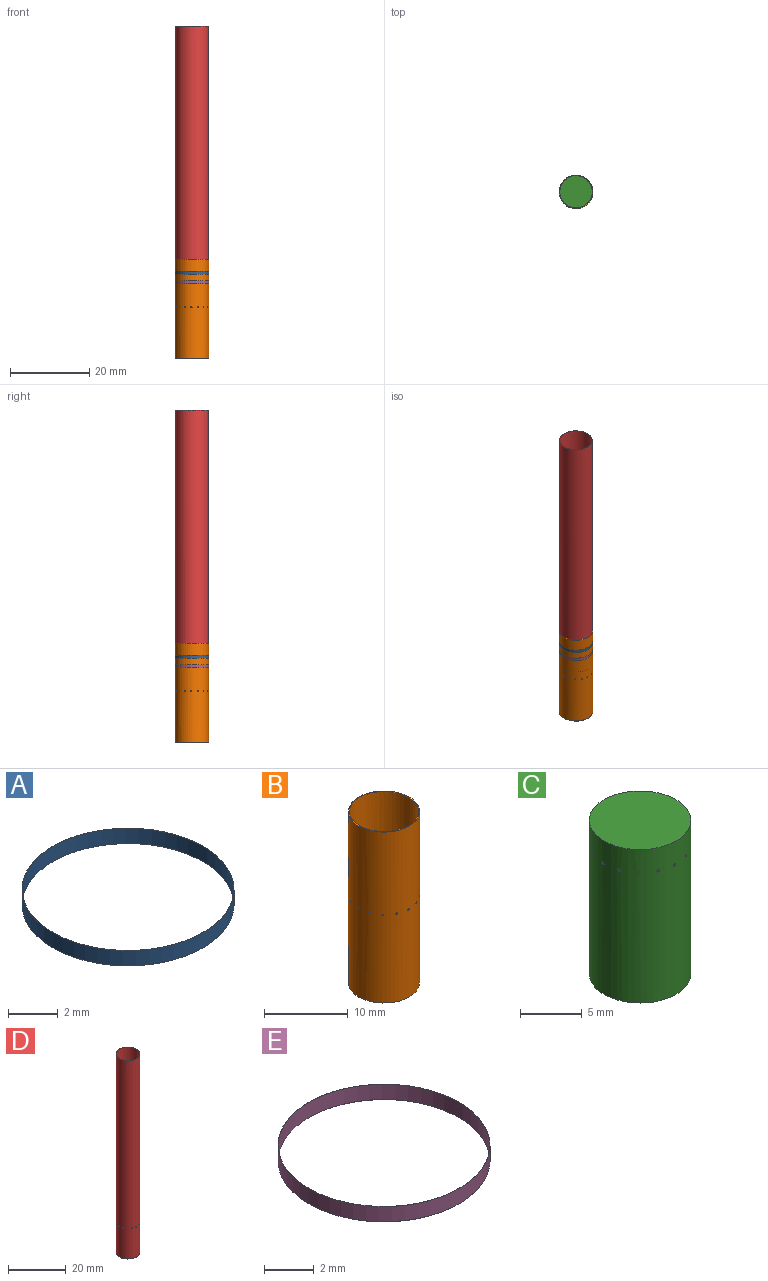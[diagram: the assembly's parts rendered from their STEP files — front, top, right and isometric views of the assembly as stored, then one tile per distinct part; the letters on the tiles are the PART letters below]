
ASSEMBLY  parts=5 mates=4
PART A: 4 faces, bbox 8.5x8.5x0.8 mm
  f0: cylinder r=4.25mm len=8.5mm, axis (0,0,-1), area 20mm2, adj f2,f3
  f1: cylinder r=4.26mm len=8.52mm, axis (0,0,-1), area 20.1mm2, adj f2,f3
  f2: plane 8.52x8.52mm, normal (0,0,1), area 0.3mm2, adj f0,f1
  f3: plane 8.52x8.52mm, normal (0,0,-1), area 0.3mm2, adj f0,f1
PART B: 68 faces, bbox 8.5x8.5x25 mm
  f0: cylinder r=4.14mm len=25mm, axis (0,0,-1), area 649.5mm2, adj f2,f3,f4,f5,f6,f7,f8,f9
  f1: cylinder r=4.25mm len=25mm, axis (0,0,-1), area 666.8mm2, adj f2,f3,f4,f5,f6,f7,f8,f9
  f2: plane 8.5x8.5mm, normal (0,0,1), area 2.9mm2, adj f0,f1
  f3: plane 8.5x8.5mm, normal (0,0,-1), area 2.9mm2, adj f0,f1
  f4: cylinder r=0.16mm len=0.15mm, axis (-0.07,-1,0), area 0mm2, adj f0,f1,f5,f6
  f5: cylinder r=0.16mm len=0.15mm, axis (0.07,1,0), area 0mm2, adj f0,f1,f4,f7
  f6: cylinder r=0.16mm len=0.14mm, axis (0,1,0), area 0mm2, adj f0,f1,f4,f7
  f7: cylinder r=0.16mm len=0.14mm, axis (0,-1,0), area 0mm2, adj f0,f1,f5,f6
  f8: cylinder r=0.16mm len=0.18mm, axis (-0.45,-0.89,0), area 0mm2, adj f0,f1,f9,f10
  f9: cylinder r=0.16mm len=0.18mm, axis (0.45,0.89,0), area 0mm2, adj f0,f1,f8,f11
  f10: cylinder r=0.16mm len=0.18mm, axis (0.38,0.92,0), area 0mm2, adj f0,f1,f8,f11
  f11: cylinder r=0.16mm len=0.18mm, axis (-0.38,-0.92,0), area 0mm2, adj f0,f1,f9,f10
  f12: cylinder r=0.16mm len=0.18mm, axis (-0.75,-0.66,0), area 0mm2, adj f0,f1,f13,f14
  f13: cylinder r=0.16mm len=0.18mm, axis (0.75,0.66,0), area 0mm2, adj f0,f1,f12,f15
  f14: cylinder r=0.16mm len=0.18mm, axis (0.71,0.71,0), area 0mm2, adj f0,f1,f12,f15
  f15: cylinder r=0.16mm len=0.18mm, axis (-0.71,-0.71,0), area 0mm2, adj f0,f1,f13,f14
  f16: cylinder r=0.16mm len=0.17mm, axis (-0.95,-0.32,0), area 0mm2, adj f0,f1,f17,f18
  f17: cylinder r=0.16mm len=0.17mm, axis (0.95,0.32,0), area 0mm2, adj f0,f1,f16,f19
  f18: cylinder r=0.16mm len=0.18mm, axis (0.92,0.38,0), area 0mm2, adj f0,f1,f16,f19
  f19: cylinder r=0.16mm len=0.18mm, axis (-0.92,-0.38,0), area 0mm2, adj f0,f1,f17,f18
  f20: cylinder r=0.16mm len=0.15mm, axis (-1,0.07,0), area 0mm2, adj f0,f1,f21,f22
  f21: cylinder r=0.16mm len=0.15mm, axis (1,-0.07,0), area 0mm2, adj f0,f1,f20,f23
  f22: cylinder r=0.16mm len=0.14mm, axis (1,0,0), area 0mm2, adj f0,f1,f20,f23
  f23: cylinder r=0.16mm len=0.14mm, axis (-1,0,0), area 0mm2, adj f0,f1,f21,f22
  f24: cylinder r=0.16mm len=0.18mm, axis (-0.89,0.45,0), area 0mm2, adj f0,f1,f25,f26
  f25: cylinder r=0.16mm len=0.18mm, axis (0.89,-0.45,0), area 0mm2, adj f0,f1,f24,f27
  f26: cylinder r=0.16mm len=0.18mm, axis (0.92,-0.38,0), area 0mm2, adj f0,f1,f24,f27
  f27: cylinder r=0.16mm len=0.18mm, axis (-0.92,0.38,0), area 0mm2, adj f0,f1,f25,f26
  f28: cylinder r=0.16mm len=0.18mm, axis (-0.66,0.75,0), area 0mm2, adj f0,f1,f29,f30
  f29: cylinder r=0.16mm len=0.18mm, axis (0.66,-0.75,0), area 0mm2, adj f0,f1,f28,f31
  f30: cylinder r=0.16mm len=0.18mm, axis (0.71,-0.71,0), area 0mm2, adj f0,f1,f28,f31
  f31: cylinder r=0.16mm len=0.18mm, axis (-0.71,0.71,0), area 0mm2, adj f0,f1,f29,f30
  f32: cylinder r=0.16mm len=0.17mm, axis (-0.32,0.95,0), area 0mm2, adj f0,f1,f33,f34
  f33: cylinder r=0.16mm len=0.17mm, axis (0.32,-0.95,0), area 0mm2, adj f0,f1,f32,f35
  f34: cylinder r=0.16mm len=0.18mm, axis (0.38,-0.92,0), area 0mm2, adj f0,f1,f32,f35
  f35: cylinder r=0.16mm len=0.18mm, axis (-0.38,0.92,0), area 0mm2, adj f0,f1,f33,f34
  f36: cylinder r=0.16mm len=0.15mm, axis (0.07,1,0), area 0mm2, adj f0,f1,f37,f38
  f37: cylinder r=0.16mm len=0.15mm, axis (-0.07,-1,0), area 0mm2, adj f0,f1,f36,f39
  f38: cylinder r=0.16mm len=0.14mm, axis (0,-1,0), area 0mm2, adj f0,f1,f36,f39
  f39: cylinder r=0.16mm len=0.14mm, axis (0,1,0), area 0mm2, adj f0,f1,f37,f38
  f40: cylinder r=0.16mm len=0.18mm, axis (0.45,0.89,0), area 0mm2, adj f0,f1,f41,f42
  f41: cylinder r=0.16mm len=0.18mm, axis (-0.45,-0.89,0), area 0mm2, adj f0,f1,f40,f43
  f42: cylinder r=0.16mm len=0.18mm, axis (-0.38,-0.92,0), area 0mm2, adj f0,f1,f40,f43
  f43: cylinder r=0.16mm len=0.18mm, axis (0.38,0.92,0), area 0mm2, adj f0,f1,f41,f42
  f44: cylinder r=0.16mm len=0.18mm, axis (0.75,0.66,0), area 0mm2, adj f0,f1,f45,f46
  f45: cylinder r=0.16mm len=0.18mm, axis (-0.75,-0.66,0), area 0mm2, adj f0,f1,f44,f47
  f46: cylinder r=0.16mm len=0.18mm, axis (-0.71,-0.71,0), area 0mm2, adj f0,f1,f44,f47
  f47: cylinder r=0.16mm len=0.18mm, axis (0.71,0.71,0), area 0mm2, adj f0,f1,f45,f46
  f48: cylinder r=0.16mm len=0.17mm, axis (0.95,0.32,0), area 0mm2, adj f0,f1,f49,f50
  f49: cylinder r=0.16mm len=0.17mm, axis (-0.95,-0.32,0), area 0mm2, adj f0,f1,f48,f51
  f50: cylinder r=0.16mm len=0.18mm, axis (-0.92,-0.38,0), area 0mm2, adj f0,f1,f48,f51
  f51: cylinder r=0.16mm len=0.18mm, axis (0.92,0.38,0), area 0mm2, adj f0,f1,f49,f50
  f52: cylinder r=0.16mm len=0.15mm, axis (1,-0.07,0), area 0mm2, adj f0,f1,f53,f54
  f53: cylinder r=0.16mm len=0.15mm, axis (-1,0.07,0), area 0mm2, adj f0,f1,f52,f55
  f54: cylinder r=0.16mm len=0.14mm, axis (-1,0,0), area 0mm2, adj f0,f1,f52,f55
  f55: cylinder r=0.16mm len=0.14mm, axis (1,0,0), area 0mm2, adj f0,f1,f53,f54
  f56: cylinder r=0.16mm len=0.18mm, axis (0.89,-0.45,0), area 0mm2, adj f0,f1,f57,f58
  f57: cylinder r=0.16mm len=0.18mm, axis (-0.89,0.45,0), area 0mm2, adj f0,f1,f56,f59
  f58: cylinder r=0.16mm len=0.18mm, axis (-0.92,0.38,0), area 0mm2, adj f0,f1,f56,f59
  f59: cylinder r=0.16mm len=0.18mm, axis (0.92,-0.38,0), area 0mm2, adj f0,f1,f57,f58
  f60: cylinder r=0.16mm len=0.18mm, axis (0.66,-0.75,0), area 0mm2, adj f0,f1,f61,f62
  f61: cylinder r=0.16mm len=0.18mm, axis (-0.66,0.75,0), area 0mm2, adj f0,f1,f60,f63
  f62: cylinder r=0.16mm len=0.18mm, axis (-0.71,0.71,0), area 0mm2, adj f0,f1,f60,f63
  f63: cylinder r=0.16mm len=0.18mm, axis (0.71,-0.71,0), area 0mm2, adj f0,f1,f61,f62
  f64: cylinder r=0.16mm len=0.17mm, axis (0.32,-0.95,0), area 0mm2, adj f0,f1,f65,f66
  f65: cylinder r=0.16mm len=0.17mm, axis (-0.32,0.95,0), area 0mm2, adj f0,f1,f64,f67
  f66: cylinder r=0.16mm len=0.18mm, axis (-0.38,0.92,0), area 0mm2, adj f0,f1,f64,f67
  f67: cylinder r=0.16mm len=0.18mm, axis (0.38,-0.92,0), area 0mm2, adj f0,f1,f65,f66
PART C: 83 faces, bbox 8.2x8.2x15.2 mm
  f0: cylinder r=4.1mm len=15.15mm, axis (0,0,1), area 389.5mm2, adj f1,f2,f4,f5,f6,f7,f9,f10
  f1: plane 8.2x8.2mm, normal (0,0,-1), area 52.8mm2, adj f0
  f2: plane 8.2x8.2mm, normal (0,0,1), area 52.8mm2, adj f0
  f3: cylinder r=4.05mm len=0.27mm, axis (0,0,1), area 0mm2, adj f4,f5,f6,f7
  f4: cylinder r=0.16mm len=0.14mm, axis (-0.07,-1,0), area 0mm2, adj f0,f3,f5,f6
  f5: cylinder r=0.16mm len=0.14mm, axis (0.07,1,0), area 0mm2, adj f0,f3,f4,f7
  f6: cylinder r=0.16mm len=0.14mm, axis (0,1,0), area 0mm2, adj f0,f3,f4,f7
  f7: cylinder r=0.16mm len=0.14mm, axis (0,-1,0), area 0mm2, adj f0,f3,f5,f6
  f8: cylinder r=4.05mm len=0.25mm, axis (0,0,1), area 0mm2, adj f9,f10,f11,f12
  f9: cylinder r=0.16mm len=0.15mm, axis (-0.45,-0.89,0), area 0mm2, adj f0,f8,f10,f11
  f10: cylinder r=0.16mm len=0.15mm, axis (0.45,0.89,0), area 0mm2, adj f0,f8,f9,f12
  f11: cylinder r=0.16mm len=0.15mm, axis (0.38,0.92,0), area 0mm2, adj f0,f8,f9,f12
  f12: cylinder r=0.16mm len=0.15mm, axis (-0.38,-0.92,0), area 0mm2, adj f0,f8,f10,f11
  f13: cylinder r=4.05mm len=0.25mm, axis (0,0,1), area 0mm2, adj f14,f15,f16,f17
  f14: cylinder r=0.16mm len=0.14mm, axis (-0.75,-0.66,0), area 0mm2, adj f0,f13,f15,f16
  f15: cylinder r=0.16mm len=0.14mm, axis (0.75,0.66,0), area 0mm2, adj f0,f13,f14,f17
  f16: cylinder r=0.16mm len=0.14mm, axis (0.71,0.71,0), area 0mm2, adj f0,f13,f14,f17
  f17: cylinder r=0.16mm len=0.14mm, axis (-0.71,-0.71,0), area 0mm2, adj f0,f13,f15,f16
  f18: cylinder r=4.05mm len=0.26mm, axis (0,0,1), area 0mm2, adj f19,f20,f21,f22
  f19: cylinder r=0.16mm len=0.15mm, axis (-0.95,-0.32,0), area 0mm2, adj f0,f18,f20,f21
  f20: cylinder r=0.16mm len=0.15mm, axis (0.95,0.32,0), area 0mm2, adj f0,f18,f19,f22
  f21: cylinder r=0.16mm len=0.15mm, axis (0.92,0.38,0), area 0mm2, adj f0,f18,f19,f22
  f22: cylinder r=0.16mm len=0.15mm, axis (-0.92,-0.38,0), area 0mm2, adj f0,f18,f20,f21
  f23: cylinder r=4.05mm len=0.27mm, axis (0,0,1), area 0mm2, adj f24,f25,f26,f27
  f24: cylinder r=0.16mm len=0.14mm, axis (-1,0.07,0), area 0mm2, adj f0,f23,f25,f26
  f25: cylinder r=0.16mm len=0.14mm, axis (1,-0.07,0), area 0mm2, adj f0,f23,f24,f27
  f26: cylinder r=0.16mm len=0.14mm, axis (1,0,0), area 0mm2, adj f0,f23,f24,f27
  f27: cylinder r=0.16mm len=0.14mm, axis (-1,0,0), area 0mm2, adj f0,f23,f25,f26
  f28: cylinder r=4.05mm len=0.25mm, axis (0,0,1), area 0mm2, adj f29,f30,f31,f32
  f29: cylinder r=0.16mm len=0.15mm, axis (-0.89,0.45,0), area 0mm2, adj f0,f28,f30,f31
  f30: cylinder r=0.16mm len=0.15mm, axis (0.89,-0.45,0), area 0mm2, adj f0,f28,f29,f32
  f31: cylinder r=0.16mm len=0.15mm, axis (0.92,-0.38,0), area 0mm2, adj f0,f28,f29,f32
  f32: cylinder r=0.16mm len=0.15mm, axis (-0.92,0.38,0), area 0mm2, adj f0,f28,f30,f31
  f33: cylinder r=4.05mm len=0.25mm, axis (0,0,1), area 0mm2, adj f34,f35,f36,f37
  f34: cylinder r=0.16mm len=0.14mm, axis (-0.66,0.75,0), area 0mm2, adj f0,f33,f35,f36
  f35: cylinder r=0.16mm len=0.14mm, axis (0.66,-0.75,0), area 0mm2, adj f0,f33,f34,f37
  f36: cylinder r=0.16mm len=0.14mm, axis (0.71,-0.71,0), area 0mm2, adj f0,f33,f34,f37
  f37: cylinder r=0.16mm len=0.14mm, axis (-0.71,0.71,0), area 0mm2, adj f0,f33,f35,f36
  f38: cylinder r=4.05mm len=0.26mm, axis (0,0,1), area 0mm2, adj f39,f40,f41,f42
  f39: cylinder r=0.16mm len=0.15mm, axis (-0.32,0.95,0), area 0mm2, adj f0,f38,f40,f41
  f40: cylinder r=0.16mm len=0.15mm, axis (0.32,-0.95,0), area 0mm2, adj f0,f38,f39,f42
  f41: cylinder r=0.16mm len=0.15mm, axis (0.38,-0.92,0), area 0mm2, adj f0,f38,f39,f42
  f42: cylinder r=0.16mm len=0.15mm, axis (-0.38,0.92,0), area 0mm2, adj f0,f38,f40,f41
  f43: cylinder r=4.05mm len=0.27mm, axis (0,0,1), area 0mm2, adj f44,f45,f46,f47
  f44: cylinder r=0.16mm len=0.14mm, axis (0.07,1,0), area 0mm2, adj f0,f43,f45,f46
  f45: cylinder r=0.16mm len=0.14mm, axis (-0.07,-1,0), area 0mm2, adj f0,f43,f44,f47
  f46: cylinder r=0.16mm len=0.14mm, axis (0,-1,0), area 0mm2, adj f0,f43,f44,f47
  f47: cylinder r=0.16mm len=0.14mm, axis (0,1,0), area 0mm2, adj f0,f43,f45,f46
  f48: cylinder r=4.05mm len=0.25mm, axis (0,0,1), area 0mm2, adj f49,f50,f51,f52
  f49: cylinder r=0.16mm len=0.15mm, axis (0.45,0.89,0), area 0mm2, adj f0,f48,f50,f51
  f50: cylinder r=0.16mm len=0.15mm, axis (-0.45,-0.89,0), area 0mm2, adj f0,f48,f49,f52
  f51: cylinder r=0.16mm len=0.15mm, axis (-0.38,-0.92,0), area 0mm2, adj f0,f48,f49,f52
  f52: cylinder r=0.16mm len=0.15mm, axis (0.38,0.92,0), area 0mm2, adj f0,f48,f50,f51
  f53: cylinder r=4.05mm len=0.25mm, axis (0,0,1), area 0mm2, adj f54,f55,f56,f57
  f54: cylinder r=0.16mm len=0.14mm, axis (0.75,0.66,0), area 0mm2, adj f0,f53,f55,f56
  f55: cylinder r=0.16mm len=0.14mm, axis (-0.75,-0.66,0), area 0mm2, adj f0,f53,f54,f57
  f56: cylinder r=0.16mm len=0.14mm, axis (-0.71,-0.71,0), area 0mm2, adj f0,f53,f54,f57
  f57: cylinder r=0.16mm len=0.14mm, axis (0.71,0.71,0), area 0mm2, adj f0,f53,f55,f56
  f58: cylinder r=4.05mm len=0.26mm, axis (0,0,1), area 0mm2, adj f59,f60,f61,f62
  f59: cylinder r=0.16mm len=0.15mm, axis (0.95,0.32,0), area 0mm2, adj f0,f58,f60,f61
  f60: cylinder r=0.16mm len=0.15mm, axis (-0.95,-0.32,0), area 0mm2, adj f0,f58,f59,f62
  f61: cylinder r=0.16mm len=0.15mm, axis (-0.92,-0.38,0), area 0mm2, adj f0,f58,f59,f62
  f62: cylinder r=0.16mm len=0.15mm, axis (0.92,0.38,0), area 0mm2, adj f0,f58,f60,f61
  f63: cylinder r=4.05mm len=0.27mm, axis (0,0,1), area 0mm2, adj f64,f65,f66,f67
  f64: cylinder r=0.16mm len=0.14mm, axis (1,-0.07,0), area 0mm2, adj f0,f63,f65,f66
  f65: cylinder r=0.16mm len=0.14mm, axis (-1,0.07,0), area 0mm2, adj f0,f63,f64,f67
  f66: cylinder r=0.16mm len=0.14mm, axis (-1,0,0), area 0mm2, adj f0,f63,f64,f67
  f67: cylinder r=0.16mm len=0.14mm, axis (1,0,0), area 0mm2, adj f0,f63,f65,f66
  f68: cylinder r=4.05mm len=0.25mm, axis (0,0,1), area 0mm2, adj f69,f70,f71,f72
  f69: cylinder r=0.16mm len=0.15mm, axis (0.89,-0.45,0), area 0mm2, adj f0,f68,f70,f71
  f70: cylinder r=0.16mm len=0.15mm, axis (-0.89,0.45,0), area 0mm2, adj f0,f68,f69,f72
  f71: cylinder r=0.16mm len=0.15mm, axis (-0.92,0.38,0), area 0mm2, adj f0,f68,f69,f72
  f72: cylinder r=0.16mm len=0.15mm, axis (0.92,-0.38,0), area 0mm2, adj f0,f68,f70,f71
  f73: cylinder r=4.05mm len=0.25mm, axis (0,0,1), area 0mm2, adj f74,f75,f76,f77
  f74: cylinder r=0.16mm len=0.14mm, axis (0.66,-0.75,0), area 0mm2, adj f0,f73,f75,f76
  f75: cylinder r=0.16mm len=0.14mm, axis (-0.66,0.75,0), area 0mm2, adj f0,f73,f74,f77
  f76: cylinder r=0.16mm len=0.14mm, axis (-0.71,0.71,0), area 0mm2, adj f0,f73,f74,f77
  f77: cylinder r=0.16mm len=0.14mm, axis (0.71,-0.71,0), area 0mm2, adj f0,f73,f75,f76
  f78: cylinder r=4.05mm len=0.26mm, axis (0,0,1), area 0mm2, adj f79,f80,f81,f82
  f79: cylinder r=0.16mm len=0.15mm, axis (0.32,-0.95,0), area 0mm2, adj f0,f78,f80,f81
  f80: cylinder r=0.16mm len=0.15mm, axis (-0.32,0.95,0), area 0mm2, adj f0,f78,f79,f82
  f81: cylinder r=0.16mm len=0.15mm, axis (-0.38,0.92,0), area 0mm2, adj f0,f78,f79,f82
  f82: cylinder r=0.16mm len=0.15mm, axis (0.38,-0.92,0), area 0mm2, adj f0,f78,f80,f81
PART D: 68 faces, bbox 8.3x8.3x84 mm
  f0: cylinder r=4.1mm len=84mm, axis (0,0,-1), area 2163.1mm2, adj f2,f3,f4,f5,f6,f7,f8,f9
  f1: cylinder r=4.14mm len=84mm, axis (0,0,-1), area 2184.2mm2, adj f2,f3,f4,f5,f6,f7,f8,f9
  f2: plane 8.28x8.28mm, normal (0,0,1), area 1mm2, adj f0,f1
  f3: plane 8.28x8.28mm, normal (0,0,-1), area 1mm2, adj f0,f1
  f4: cylinder r=0.16mm len=0.14mm, axis (-0.07,-1,0), area 0mm2, adj f0,f1,f5,f6
  f5: cylinder r=0.16mm len=0.14mm, axis (0.07,1,0), area 0mm2, adj f0,f1,f4,f7
  f6: cylinder r=0.16mm len=0.14mm, axis (0,1,0), area 0mm2, adj f0,f1,f4,f7
  f7: cylinder r=0.16mm len=0.14mm, axis (0,-1,0), area 0mm2, adj f0,f1,f5,f6
  f8: cylinder r=0.16mm len=0.14mm, axis (-0.45,-0.89,0), area 0mm2, adj f0,f1,f9,f10
  f9: cylinder r=0.16mm len=0.14mm, axis (0.45,0.89,0), area 0mm2, adj f0,f1,f8,f11
  f10: cylinder r=0.16mm len=0.15mm, axis (0.38,0.92,0), area 0mm2, adj f0,f1,f8,f11
  f11: cylinder r=0.16mm len=0.15mm, axis (-0.38,-0.92,0), area 0mm2, adj f0,f1,f9,f10
  f12: cylinder r=0.16mm len=0.13mm, axis (-0.75,-0.66,0), area 0mm2, adj f0,f1,f13,f14
  f13: cylinder r=0.16mm len=0.13mm, axis (0.75,0.66,0), area 0mm2, adj f0,f1,f12,f15
  f14: cylinder r=0.16mm len=0.13mm, axis (0.71,0.71,0), area 0mm2, adj f0,f1,f12,f15
  f15: cylinder r=0.16mm len=0.13mm, axis (-0.71,-0.71,0), area 0mm2, adj f0,f1,f13,f14
  f16: cylinder r=0.16mm len=0.15mm, axis (-0.95,-0.32,0), area 0mm2, adj f0,f1,f17,f18
  f17: cylinder r=0.16mm len=0.15mm, axis (0.95,0.32,0), area 0mm2, adj f0,f1,f16,f19
  f18: cylinder r=0.16mm len=0.15mm, axis (0.92,0.38,0), area 0mm2, adj f0,f1,f16,f19
  f19: cylinder r=0.16mm len=0.15mm, axis (-0.92,-0.38,0), area 0mm2, adj f0,f1,f17,f18
  f20: cylinder r=0.16mm len=0.14mm, axis (-1,0.07,0), area 0mm2, adj f0,f1,f21,f22
  f21: cylinder r=0.16mm len=0.14mm, axis (1,-0.07,0), area 0mm2, adj f0,f1,f20,f23
  f22: cylinder r=0.16mm len=0.14mm, axis (1,0,0), area 0mm2, adj f0,f1,f20,f23
  f23: cylinder r=0.16mm len=0.14mm, axis (-1,0,0), area 0mm2, adj f0,f1,f21,f22
  f24: cylinder r=0.16mm len=0.14mm, axis (-0.89,0.45,0), area 0mm2, adj f0,f1,f25,f26
  f25: cylinder r=0.16mm len=0.14mm, axis (0.89,-0.45,0), area 0mm2, adj f0,f1,f24,f27
  f26: cylinder r=0.16mm len=0.15mm, axis (0.92,-0.38,0), area 0mm2, adj f0,f1,f24,f27
  f27: cylinder r=0.16mm len=0.15mm, axis (-0.92,0.38,0), area 0mm2, adj f0,f1,f25,f26
  f28: cylinder r=0.16mm len=0.13mm, axis (-0.66,0.75,0), area 0mm2, adj f0,f1,f29,f30
  f29: cylinder r=0.16mm len=0.13mm, axis (0.66,-0.75,0), area 0mm2, adj f0,f1,f28,f31
  f30: cylinder r=0.16mm len=0.13mm, axis (0.71,-0.71,0), area 0mm2, adj f0,f1,f28,f31
  f31: cylinder r=0.16mm len=0.13mm, axis (-0.71,0.71,0), area 0mm2, adj f0,f1,f29,f30
  f32: cylinder r=0.16mm len=0.15mm, axis (-0.32,0.95,0), area 0mm2, adj f0,f1,f33,f34
  f33: cylinder r=0.16mm len=0.15mm, axis (0.32,-0.95,0), area 0mm2, adj f0,f1,f32,f35
  f34: cylinder r=0.16mm len=0.15mm, axis (0.38,-0.92,0), area 0mm2, adj f0,f1,f32,f35
  f35: cylinder r=0.16mm len=0.15mm, axis (-0.38,0.92,0), area 0mm2, adj f0,f1,f33,f34
  f36: cylinder r=0.16mm len=0.14mm, axis (0.07,1,0), area 0mm2, adj f0,f1,f37,f38
  f37: cylinder r=0.16mm len=0.14mm, axis (-0.07,-1,0), area 0mm2, adj f0,f1,f36,f39
  f38: cylinder r=0.16mm len=0.14mm, axis (0,-1,0), area 0mm2, adj f0,f1,f36,f39
  f39: cylinder r=0.16mm len=0.14mm, axis (0,1,0), area 0mm2, adj f0,f1,f37,f38
  f40: cylinder r=0.16mm len=0.14mm, axis (0.45,0.89,0), area 0mm2, adj f0,f1,f41,f42
  f41: cylinder r=0.16mm len=0.14mm, axis (-0.45,-0.89,0), area 0mm2, adj f0,f1,f40,f43
  f42: cylinder r=0.16mm len=0.15mm, axis (-0.38,-0.92,0), area 0mm2, adj f0,f1,f40,f43
  f43: cylinder r=0.16mm len=0.15mm, axis (0.38,0.92,0), area 0mm2, adj f0,f1,f41,f42
  f44: cylinder r=0.16mm len=0.13mm, axis (0.75,0.66,0), area 0mm2, adj f0,f1,f45,f46
  f45: cylinder r=0.16mm len=0.13mm, axis (-0.75,-0.66,0), area 0mm2, adj f0,f1,f44,f47
  f46: cylinder r=0.16mm len=0.13mm, axis (-0.71,-0.71,0), area 0mm2, adj f0,f1,f44,f47
  f47: cylinder r=0.16mm len=0.13mm, axis (0.71,0.71,0), area 0mm2, adj f0,f1,f45,f46
  f48: cylinder r=0.16mm len=0.15mm, axis (0.95,0.32,0), area 0mm2, adj f0,f1,f49,f50
  f49: cylinder r=0.16mm len=0.15mm, axis (-0.95,-0.32,0), area 0mm2, adj f0,f1,f48,f51
  f50: cylinder r=0.16mm len=0.15mm, axis (-0.92,-0.38,0), area 0mm2, adj f0,f1,f48,f51
  f51: cylinder r=0.16mm len=0.15mm, axis (0.92,0.38,0), area 0mm2, adj f0,f1,f49,f50
  f52: cylinder r=0.16mm len=0.14mm, axis (1,-0.07,0), area 0mm2, adj f0,f1,f53,f54
  f53: cylinder r=0.16mm len=0.14mm, axis (-1,0.07,0), area 0mm2, adj f0,f1,f52,f55
  f54: cylinder r=0.16mm len=0.14mm, axis (-1,0,0), area 0mm2, adj f0,f1,f52,f55
  f55: cylinder r=0.16mm len=0.14mm, axis (1,0,0), area 0mm2, adj f0,f1,f53,f54
  f56: cylinder r=0.16mm len=0.14mm, axis (0.89,-0.45,0), area 0mm2, adj f0,f1,f57,f58
  f57: cylinder r=0.16mm len=0.14mm, axis (-0.89,0.45,0), area 0mm2, adj f0,f1,f56,f59
  f58: cylinder r=0.16mm len=0.15mm, axis (-0.92,0.38,0), area 0mm2, adj f0,f1,f56,f59
  f59: cylinder r=0.16mm len=0.15mm, axis (0.92,-0.38,0), area 0mm2, adj f0,f1,f57,f58
  f60: cylinder r=0.16mm len=0.13mm, axis (0.66,-0.75,0), area 0mm2, adj f0,f1,f61,f62
  f61: cylinder r=0.16mm len=0.13mm, axis (-0.66,0.75,0), area 0mm2, adj f0,f1,f60,f63
  f62: cylinder r=0.16mm len=0.13mm, axis (-0.71,0.71,0), area 0mm2, adj f0,f1,f60,f63
  f63: cylinder r=0.16mm len=0.13mm, axis (0.71,-0.71,0), area 0mm2, adj f0,f1,f61,f62
  f64: cylinder r=0.16mm len=0.15mm, axis (0.32,-0.95,0), area 0mm2, adj f0,f1,f65,f66
  f65: cylinder r=0.16mm len=0.15mm, axis (-0.32,0.95,0), area 0mm2, adj f0,f1,f64,f67
  f66: cylinder r=0.16mm len=0.15mm, axis (-0.38,0.92,0), area 0mm2, adj f0,f1,f64,f67
  f67: cylinder r=0.16mm len=0.15mm, axis (0.38,-0.92,0), area 0mm2, adj f0,f1,f65,f66
PART E: 4 faces, bbox 8.5x8.5x0.8 mm
  f0: cylinder r=4.25mm len=8.5mm, axis (0,0,-1), area 20mm2, adj f2,f3
  f1: cylinder r=4.26mm len=8.52mm, axis (0,0,-1), area 20.1mm2, adj f2,f3
  f2: plane 8.52x8.52mm, normal (0,0,1), area 0.3mm2, adj f0,f1
  f3: plane 8.52x8.52mm, normal (0,0,-1), area 0.3mm2, adj f0,f1
PLACE A at identity
PLACE B at identity
PLACE C at identity
PLACE D at identity
PLACE E at identity
MATE fastened D.f1 <-> C.f0  axis (0,0,-1) through (0,0,-15.15)mm
MATE fastened E.f1 <-> D.f1  axis (0,0,-1) through (0,0,3.6)mm
MATE fastened A.f0 <-> D.f1  axis (0,0,-1) through (0,0,6.1)mm
MATE fastened C.f0 <-> B.f0  axis (0,0,-1) through (0,0,-15.15)mm
